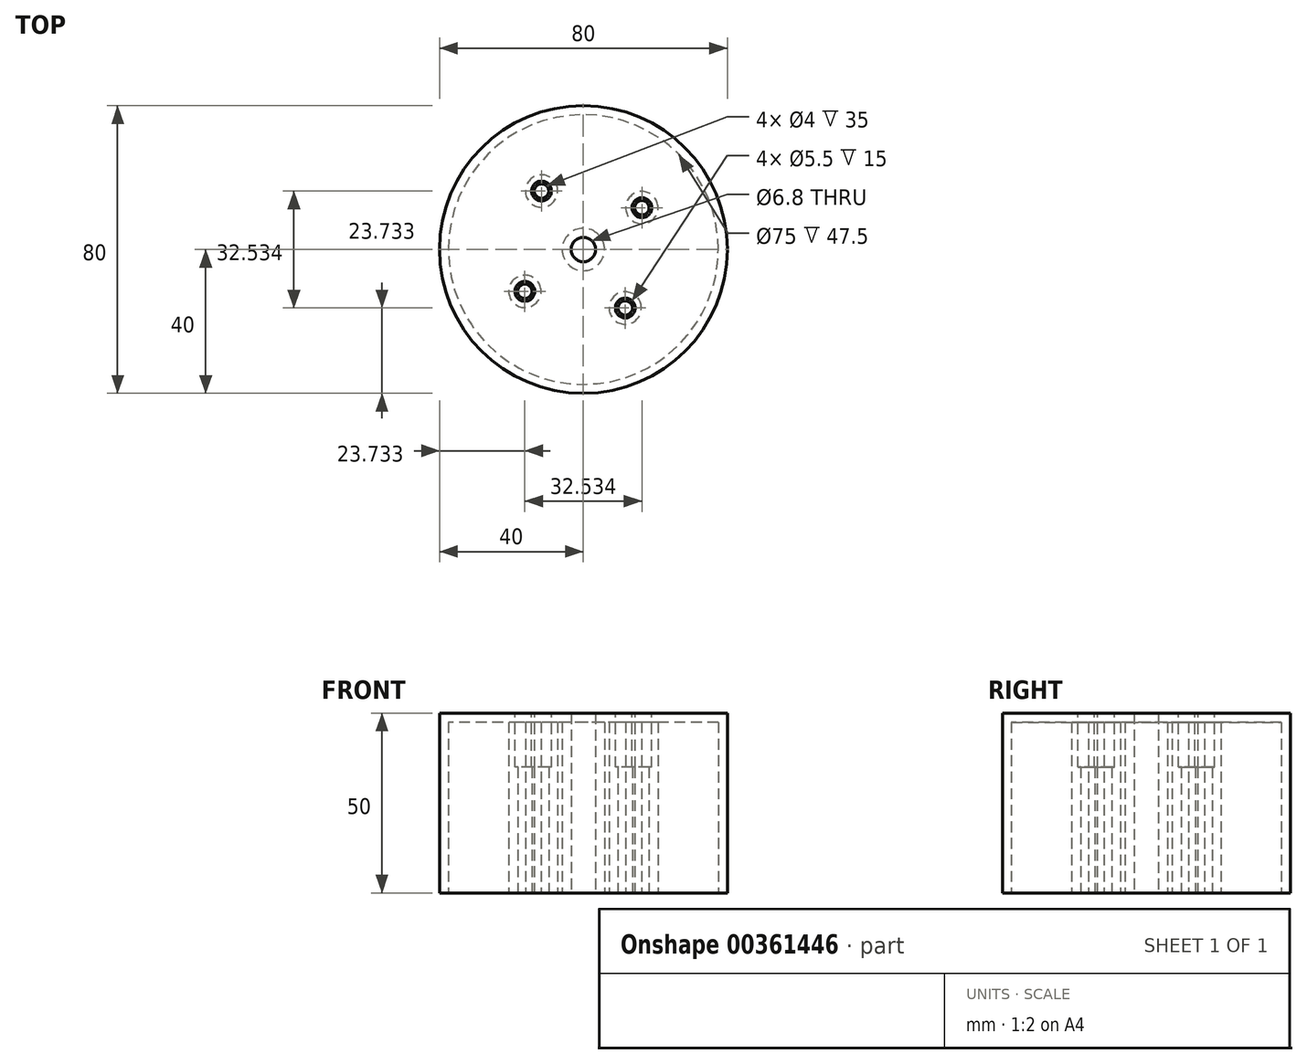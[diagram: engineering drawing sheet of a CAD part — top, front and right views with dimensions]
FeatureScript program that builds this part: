
annotation { "Feature Type Name" : "Feature", "Feature Type Description" : "" }
export const myFeature = defineFeature(function(context is Context, id is Id, definition is map)
    precondition{}
    {
        {
            var Q0;
            Q0=qCreatedBy(makeId("Top.planeOp"),FACE);
            var sketch = newSketch(context, id + "F0", { "sketchPlane" : qUnion([Q0])});
            skCircle(sketch, "E0", {"center": v(0, 0) * mm, "radius": 40 * mm});
            skLineSegment(sketch, "E1", {"start": v(0, 0) * mm, "end": v(32.53, 23.27) * mm, "construction": true});
            skLineSegment(sketch, "E2", {"start": v(16.27, 11.64) * mm, "end": v(0, 0) * mm, "construction": true});
            skCircle(sketch, "E3", {"center": v(16.27, 11.64) * mm, "radius": 2 * mm});
            skLineSegment(sketch, "E4", {"start": v(32.53, 23.27) * mm, "end": v(-32.53, -23.27) * mm, "construction": true});
            skLineSegment(sketch, "E5", {"start": v(-32.53, -23.27) * mm, "end": v(-16.27, -11.64) * mm, "construction": true});
            skCircle(sketch, "E6", {"center": v(-16.27, -11.64) * mm, "radius": 2 * mm});
            skLineSegment(sketch, "E7", {"start": v(0, 0) * mm, "end": v(23.27, -32.53) * mm, "construction": true});
            skLineSegment(sketch, "E8", {"start": v(23.27, -32.53) * mm, "end": v(-23.27, 32.53) * mm, "construction": true});
            skLineSegment(sketch, "E9", {"start": v(-23.27, 32.53) * mm, "end": v(-11.64, 16.27) * mm, "construction": true});
            skLineSegment(sketch, "E10", {"start": v(11.64, -16.27) * mm, "end": v(0, 0) * mm, "construction": true});
            skCircle(sketch, "E11", {"center": v(-11.64, 16.27) * mm, "radius": 2 * mm});
            skCircle(sketch, "E12", {"center": v(11.64, -16.27) * mm, "radius": 2 * mm});
            skCircle(sketch, "E13", {"center": v(0, 0) * mm, "radius": 3.4 * mm});
            skSolve(sketch);
        }
        {
            var Q0;
            Q0=qSketchRegion(id+"F0",true);
            extrude(context, id + "F1", {"entities" : qUnion([Q0]), "depth" : 50 * mm});
        }
        {
            var Q0;
            Q0=qCreatedBy(makeId("Top.planeOp"),FACE);
            var sketch = newSketch(context, id + "F2", { "sketchPlane" : qUnion([Q0])});
            skCircle(sketch, "E14", {"center": v(0, 0) * mm, "radius": 7.22 * mm});
            skSolve(sketch);
        }
        {
            var Q0;
            Q0=makeQuery(id+"F1.opExtrude","CAP_FACE",FACE,{"disambiguationData":[OSD([sQuery(id+"F0.wireOp",EDGE,"E0"),sQuery(id+"F0.wireOp",EDGE,"E3"),sQuery(id+"F0.wireOp",EDGE,"E6"),sQuery(id+"F0.wireOp",EDGE,"E11"),sQuery(id+"F0.wireOp",EDGE,"E12"),sQuery(id+"F0.wireOp",EDGE,"E13")])],"isStart":false});
            var sketch = newSketch(context, id + "F3", { "sketchPlane" : qUnion([Q0])});
            skCircle(sketch, "E15", {"center": v(-11.64, 16.27) * mm, "radius": 2.75 * mm});
            skCircle(sketch, "E16", {"center": v(16.27, 11.64) * mm, "radius": 2.75 * mm});
            skCircle(sketch, "E17", {"center": v(11.64, -16.27) * mm, "radius": 2.75 * mm});
            skCircle(sketch, "E18", {"center": v(-16.27, -11.64) * mm, "radius": 2.75 * mm});
            skSolve(sketch);
        }
        {
            var Q0;
            Q0=qSketchRegion(id+"F3",true);
            extrude(context, id + "F4", {"entities" : qUnion([Q0]), "oppositeDirection" : true, "depth" : 10 * mm});
        }
        {
            var Q0;
            Q0=makeQuery(id+"F1.opExtrude","CAP_FACE",FACE,{"disambiguationData":[OSD([sQuery(id+"F0.wireOp",EDGE,"E0"),sQuery(id+"F0.wireOp",EDGE,"E3"),sQuery(id+"F0.wireOp",EDGE,"E6"),sQuery(id+"F0.wireOp",EDGE,"E11"),sQuery(id+"F0.wireOp",EDGE,"E12"),sQuery(id+"F0.wireOp",EDGE,"E13")])],"isStart":true});
            shell(context, id + "F5", {"entities" : qUnion([Q0]), "thickness" : 2.5 * mm});
        }
        {
            var Q0;
            Q0=makeQuery(id+"F4.opExtrude","CAP_FACE",FACE,{"disambiguationData":[OSD([sQuery(id+"F3.wireOp",EDGE,"E15")])],"isStart":true});
            var Q1;
            Q1=makeQuery(id+"F4.opExtrude","CAP_FACE",FACE,{"disambiguationData":[OSD([sQuery(id+"F3.wireOp",EDGE,"E17")])],"isStart":true});
            var Q2;
            Q2=makeQuery(id+"F4.opExtrude","CAP_FACE",FACE,{"disambiguationData":[OSD([sQuery(id+"F3.wireOp",EDGE,"E16")])],"isStart":true});
            var Q3;
            Q3=makeQuery(id+"F4.opExtrude","CAP_FACE",FACE,{"disambiguationData":[OSD([sQuery(id+"F3.wireOp",EDGE,"E18")])],"isStart":true});
            extrude(context, id + "F6", {"entities" : qUnion([Q0, Q1, Q2, Q3]), "operationType" : NewBodyOperationType.REMOVE, "oppositeDirection" : true, "depth" : 15 * mm});
        }
    });
